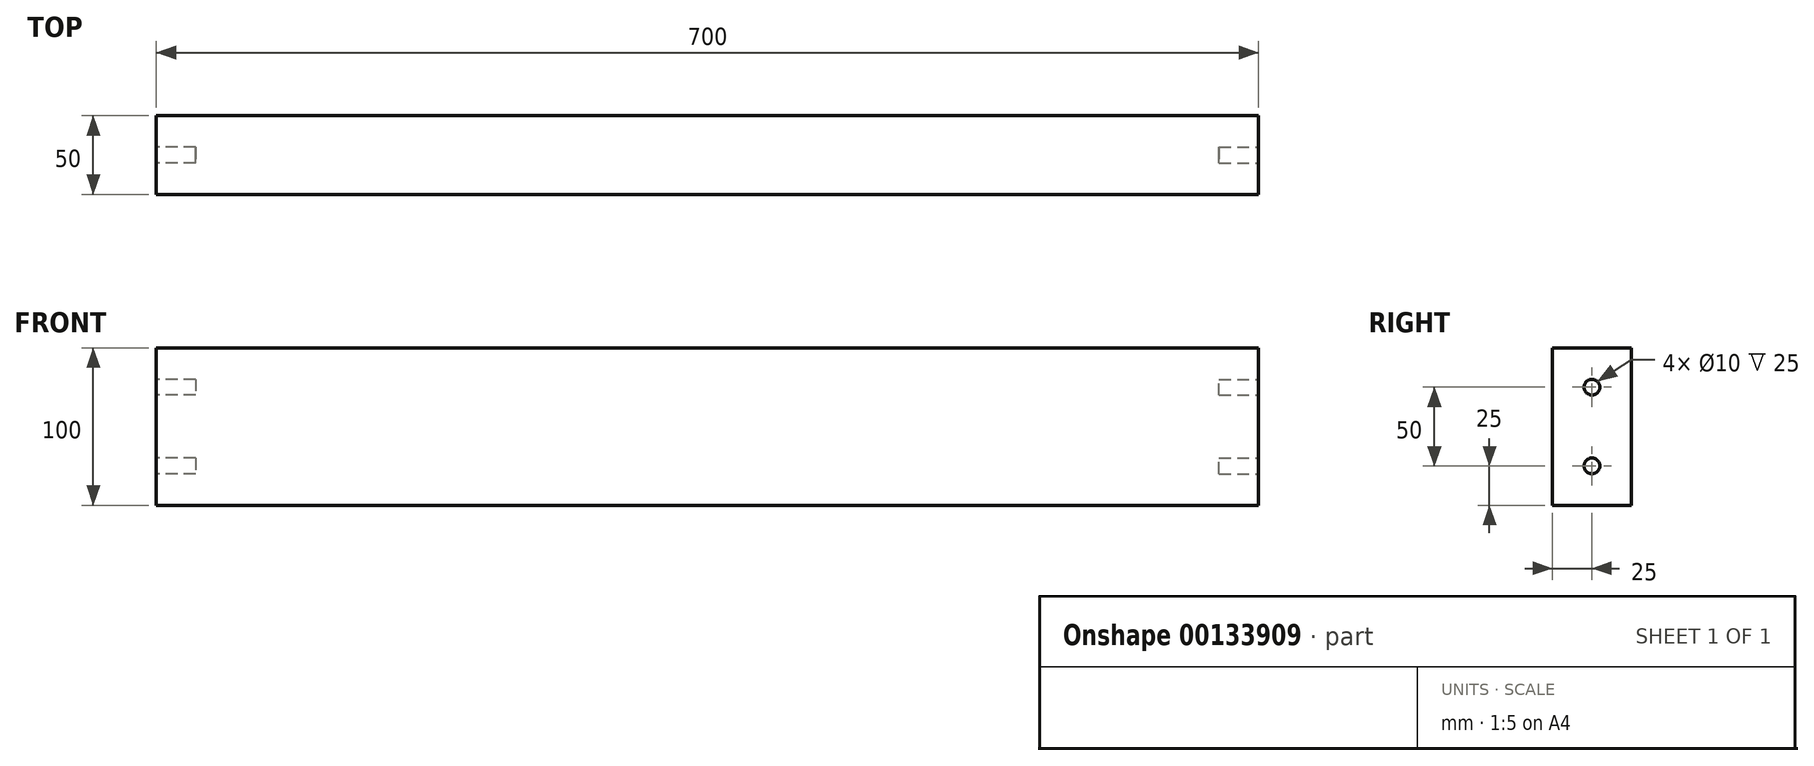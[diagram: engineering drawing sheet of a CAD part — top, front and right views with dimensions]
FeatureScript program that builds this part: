
annotation { "Feature Type Name" : "Feature", "Feature Type Description" : "" }
export const myFeature = defineFeature(function(context is Context, id is Id, definition is map)
    precondition{}
    {
        {
            var Q0;
            Q0=qCreatedBy(makeId("Front.planeOp"),FACE);
            var sketch = newSketch(context, id + "F0", { "sketchPlane" : qUnion([Q0])});
            skLineSegment(sketch, "E0.bottom", {"start": v(350, -50) * mm, "end": v(-350, -50) * mm});
            skLineSegment(sketch, "E0.top", {"start": v(350, 50) * mm, "end": v(-350, 50) * mm});
            skLineSegment(sketch, "E0.left", {"start": v(350, -50) * mm, "end": v(350, 50) * mm});
            skLineSegment(sketch, "E0.right", {"start": v(-350, -50) * mm, "end": v(-350, 50) * mm});
            skPoint(sketch, "E0.middle", {"position": v(0, 0) * mm});
            skSolve(sketch);
        }
        {
            var Q0;
            Q0=makeQuery(id+"F0.imprint","IMPRINT",FACE,{"disambiguationData":[TD([[makeQuery(id+"F0.imprint","IMPRINT",EDGE,{"derivedFrom":sQuery(id+"F0.wireOp",EDGE,"E0.bottom")}),-1.0]])]});
            extrude(context, id + "F1", {"entities" : qUnion([Q0]), "depth" : 50 * mm});
        }
        {
            var Q0;
            Q0=makeQuery(id+"F1.opExtrude","SWEPT_FACE",FACE,{"disambiguationData":[OSD([sQuery(id+"F0.wireOp",EDGE,"E0.left")])]});
            var sketch = newSketch(context, id + "F2", { "sketchPlane" : qUnion([Q0])});
            skCircle(sketch, "E1", {"center": v(-25, 25) * mm, "radius": 5 * mm});
            skPoint(sketch, "E1.centerSnap0", {"position": v(-25, 50) * mm});
            skCircle(sketch, "E2", {"center": v(-25, -25) * mm, "radius": 5 * mm});
            skPoint(sketch, "E2.centerSnap0", {"position": v(-25, -50) * mm});
            skSolve(sketch);
        }
        {
            var Q0;
            Q0=makeQuery(id+"F1.opExtrude","SWEPT_FACE",FACE,{"disambiguationData":[OSD([sQuery(id+"F0.wireOp",EDGE,"E0.right")])]});
            var sketch = newSketch(context, id + "F3", { "sketchPlane" : qUnion([Q0])});
            skCircle(sketch, "E3", {"center": v(25, 25) * mm, "radius": 5 * mm});
            skPoint(sketch, "E3.centerSnap0", {"position": v(25, 50) * mm});
            skCircle(sketch, "E4", {"center": v(25, -25) * mm, "radius": 5 * mm});
            skPoint(sketch, "E4.centerSnap0", {"position": v(25, -50) * mm});
            skSolve(sketch);
        }
        {
            var Q0;
            Q0=makeQuery(id+"F3.imprint","IMPRINT",FACE,{"disambiguationData":[TD([[makeQuery(id+"F3.imprint","IMPRINT",EDGE,{"derivedFrom":sQuery(id+"F3.wireOp",EDGE,"E3")}),1.0]])]});
            var Q1;
            Q1=makeQuery(id+"F3.imprint","IMPRINT",FACE,{"disambiguationData":[TD([[makeQuery(id+"F3.imprint","IMPRINT",EDGE,{"derivedFrom":sQuery(id+"F3.wireOp",EDGE,"E4")}),1.0]])]});
            extrude(context, id + "F4", {"entities" : qUnion([Q0, Q1]), "operationType" : NewBodyOperationType.REMOVE, "oppositeDirection" : true, "depth" : 25 * mm});
        }
        {
            var Q0;
            Q0=makeQuery(id+"F2.imprint","IMPRINT",FACE,{"disambiguationData":[TD([[makeQuery(id+"F2.imprint","IMPRINT",EDGE,{"derivedFrom":sQuery(id+"F2.wireOp",EDGE,"E1")}),1.0]])]});
            var Q1;
            Q1=makeQuery(id+"F2.imprint","IMPRINT",FACE,{"disambiguationData":[TD([[makeQuery(id+"F2.imprint","IMPRINT",EDGE,{"derivedFrom":sQuery(id+"F2.wireOp",EDGE,"E2")}),1.0]])]});
            extrude(context, id + "F5", {"entities" : qUnion([Q0, Q1]), "operationType" : NewBodyOperationType.REMOVE, "oppositeDirection" : true, "depth" : 25 * mm});
        }
    });
